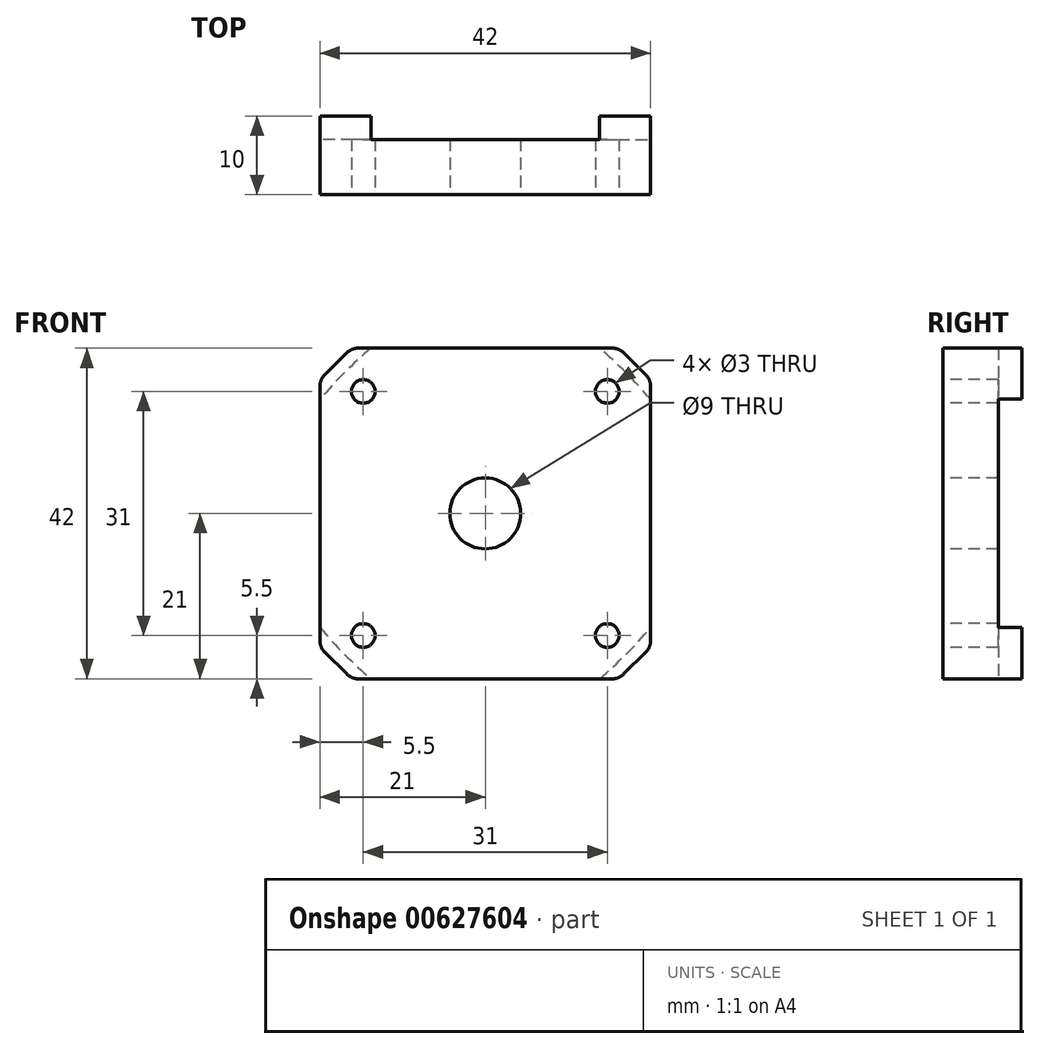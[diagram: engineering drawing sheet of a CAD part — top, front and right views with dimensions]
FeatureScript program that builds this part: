
annotation { "Feature Type Name" : "Feature", "Feature Type Description" : "" }
export const myFeature = defineFeature(function(context is Context, id is Id, definition is map)
    precondition{}
    {
        {
            var Q0;
            Q0=qCreatedBy(makeId("Front.planeOp"),FACE);
            var sketch = newSketch(context, id + "F0", { "sketchPlane" : qUnion([Q0])});
            skLineSegment(sketch, "E0.bottom", {"start": v(-21, 21) * mm, "end": v(21, 21) * mm});
            skLineSegment(sketch, "E0.top", {"start": v(-21, -21) * mm, "end": v(21, -21) * mm});
            skLineSegment(sketch, "E0.left", {"start": v(-21, 21) * mm, "end": v(-21, -21) * mm});
            skLineSegment(sketch, "E0.right", {"start": v(21, 21) * mm, "end": v(21, -21) * mm});
            skPoint(sketch, "E0.middle", {"position": v(0, 0) * mm});
            skSolve(sketch);
        }
        {
            var Q0;
            Q0=makeQuery(id+"F0.imprint","IMPRINT",FACE,{"disambiguationData":[TD([[makeQuery(id+"F0.imprint","IMPRINT",EDGE,{"derivedFrom":sQuery(id+"F0.wireOp",EDGE,"E0.bottom")}),-1.0]])]});
            extrude(context, id + "F1", {"entities" : qUnion([Q0]), "depth" : 10 * mm, "offsetDistance" : 25 * mm});
        }
        {
            var Q0;
            Q0=makeQuery(id+"F1.opExtrude","SWEPT_EDGE",EDGE,{"disambiguationData":[OSD([sQuery(id+"F0.wireOp",EDGE,"E0.bottom"),sQuery(id+"F0.wireOp",EDGE,"E0.left")])]});
            var Q1;
            Q1=makeQuery(id+"F1.opExtrude","SWEPT_EDGE",EDGE,{"disambiguationData":[OSD([sQuery(id+"F0.wireOp",EDGE,"E0.bottom"),sQuery(id+"F0.wireOp",EDGE,"E0.right")])]});
            var Q2;
            Q2=makeQuery(id+"F1.opExtrude","SWEPT_EDGE",EDGE,{"disambiguationData":[OSD([sQuery(id+"F0.wireOp",EDGE,"E0.top"),sQuery(id+"F0.wireOp",EDGE,"E0.right")])]});
            var Q3;
            Q3=makeQuery(id+"F1.opExtrude","SWEPT_EDGE",EDGE,{"disambiguationData":[OSD([sQuery(id+"F0.wireOp",EDGE,"E0.top"),sQuery(id+"F0.wireOp",EDGE,"E0.left")])]});
            chamfer(context, id + "F2", {"entities" : qUnion([Q0, Q1, Q2, Q3]), "width" : 4 * mm, "tangentPropagation" : true});
        }
        {
            var Q0;
            {var subQ0=sQuery(id+"F0.wireOp",EDGE,"E0.bottom");Q0=makeQuery(id+"F2.opChamfer","BLEND_EDGE",EDGE,{"blendedFrom":[makeQuery(id+"F1.opExtrude","SWEPT_EDGE",EDGE,{"disambiguationData":[OSD([subQ0,sQuery(id+"F0.wireOp",EDGE,"E0.left")])]}),makeQuery(id+"F1.opExtrude","SWEPT_FACE",FACE,{"disambiguationData":[OSD([subQ0])]})],"blendedInto":[makeQuery(id+"F1.opExtrude","SWEPT_FACE",FACE,{"disambiguationData":[OSD([subQ0])]})]});}
            var Q1;
            {var subQ0=sQuery(id+"F0.wireOp",EDGE,"E0.bottom");Q1=makeQuery(id+"F2.opChamfer","BLEND_EDGE",EDGE,{"blendedFrom":[makeQuery(id+"F1.opExtrude","SWEPT_EDGE",EDGE,{"disambiguationData":[OSD([subQ0,sQuery(id+"F0.wireOp",EDGE,"E0.right")])]}),makeQuery(id+"F1.opExtrude","SWEPT_FACE",FACE,{"disambiguationData":[OSD([subQ0])]})],"blendedInto":[makeQuery(id+"F1.opExtrude","SWEPT_FACE",FACE,{"disambiguationData":[OSD([subQ0])]})]});}
            var Q2;
            {var subQ0=sQuery(id+"F0.wireOp",EDGE,"E0.right");Q2=makeQuery(id+"F2.opChamfer","BLEND_EDGE",EDGE,{"blendedFrom":[makeQuery(id+"F1.opExtrude","SWEPT_EDGE",EDGE,{"disambiguationData":[OSD([sQuery(id+"F0.wireOp",EDGE,"E0.bottom"),subQ0])]}),makeQuery(id+"F1.opExtrude","SWEPT_FACE",FACE,{"disambiguationData":[OSD([subQ0])]})],"blendedInto":[makeQuery(id+"F1.opExtrude","SWEPT_FACE",FACE,{"disambiguationData":[OSD([subQ0])]})]});}
            var Q3;
            {var subQ0=sQuery(id+"F0.wireOp",EDGE,"E0.right");Q3=makeQuery(id+"F2.opChamfer","BLEND_EDGE",EDGE,{"blendedFrom":[makeQuery(id+"F1.opExtrude","SWEPT_EDGE",EDGE,{"disambiguationData":[OSD([sQuery(id+"F0.wireOp",EDGE,"E0.top"),subQ0])]}),makeQuery(id+"F1.opExtrude","SWEPT_FACE",FACE,{"disambiguationData":[OSD([subQ0])]})],"blendedInto":[makeQuery(id+"F1.opExtrude","SWEPT_FACE",FACE,{"disambiguationData":[OSD([subQ0])]})]});}
            var Q4;
            {var subQ0=sQuery(id+"F0.wireOp",EDGE,"E0.top");Q4=makeQuery(id+"F2.opChamfer","BLEND_EDGE",EDGE,{"blendedFrom":[makeQuery(id+"F1.opExtrude","SWEPT_EDGE",EDGE,{"disambiguationData":[OSD([subQ0,sQuery(id+"F0.wireOp",EDGE,"E0.right")])]}),makeQuery(id+"F1.opExtrude","SWEPT_FACE",FACE,{"disambiguationData":[OSD([subQ0])]})],"blendedInto":[makeQuery(id+"F1.opExtrude","SWEPT_FACE",FACE,{"disambiguationData":[OSD([subQ0])]})]});}
            var Q5;
            {var subQ0=sQuery(id+"F0.wireOp",EDGE,"E0.top");Q5=makeQuery(id+"F2.opChamfer","BLEND_EDGE",EDGE,{"blendedFrom":[makeQuery(id+"F1.opExtrude","SWEPT_EDGE",EDGE,{"disambiguationData":[OSD([subQ0,sQuery(id+"F0.wireOp",EDGE,"E0.left")])]}),makeQuery(id+"F1.opExtrude","SWEPT_FACE",FACE,{"disambiguationData":[OSD([subQ0])]})],"blendedInto":[makeQuery(id+"F1.opExtrude","SWEPT_FACE",FACE,{"disambiguationData":[OSD([subQ0])]})]});}
            var Q6;
            {var subQ0=sQuery(id+"F0.wireOp",EDGE,"E0.left");Q6=makeQuery(id+"F2.opChamfer","BLEND_EDGE",EDGE,{"blendedFrom":[makeQuery(id+"F1.opExtrude","SWEPT_EDGE",EDGE,{"disambiguationData":[OSD([sQuery(id+"F0.wireOp",EDGE,"E0.top"),subQ0])]}),makeQuery(id+"F1.opExtrude","SWEPT_FACE",FACE,{"disambiguationData":[OSD([subQ0])]})],"blendedInto":[makeQuery(id+"F1.opExtrude","SWEPT_FACE",FACE,{"disambiguationData":[OSD([subQ0])]})]});}
            var Q7;
            {var subQ0=sQuery(id+"F0.wireOp",EDGE,"E0.left");Q7=makeQuery(id+"F2.opChamfer","BLEND_EDGE",EDGE,{"blendedFrom":[makeQuery(id+"F1.opExtrude","SWEPT_EDGE",EDGE,{"disambiguationData":[OSD([sQuery(id+"F0.wireOp",EDGE,"E0.bottom"),subQ0])]}),makeQuery(id+"F1.opExtrude","SWEPT_FACE",FACE,{"disambiguationData":[OSD([subQ0])]})],"blendedInto":[makeQuery(id+"F1.opExtrude","SWEPT_FACE",FACE,{"disambiguationData":[OSD([subQ0])]})]});}
            fillet(context, id + "F3", {"entities" : qUnion([Q0, Q1, Q2, Q3, Q4, Q5, Q6, Q7]), "radius" : 2 * mm, "tangentPropagation" : true, "allowEdgeOverflow" : false});
        }
        {
            var Q0;
            Q0=makeQuery(id+"F1.opExtrude","CAP_FACE",FACE,{"disambiguationData":[OSD([sQuery(id+"F0.wireOp",EDGE,"E0.bottom"),sQuery(id+"F0.wireOp",EDGE,"E0.top"),sQuery(id+"F0.wireOp",EDGE,"E0.left"),sQuery(id+"F0.wireOp",EDGE,"E0.right")])],"isStart":true});
            var sketch = newSketch(context, id + "F4", { "sketchPlane" : qUnion([Q0])});
            skLineSegment(sketch, "E1.bottom", {"start": v(-21, 21) * mm, "end": v(21, 21) * mm, "construction": true});
            skLineSegment(sketch, "E1.top", {"start": v(-21, -21) * mm, "end": v(21, -21) * mm, "construction": true});
            skLineSegment(sketch, "E1.left", {"start": v(-21, 21) * mm, "end": v(-21, -21) * mm, "construction": true});
            skLineSegment(sketch, "E1.right", {"start": v(21, 21) * mm, "end": v(21, -21) * mm, "construction": true});
            skPoint(sketch, "E1.middle", {"position": v(0, 0) * mm});
            skArc(sketch, "E2", {"start": v(-21, 14.51) * mm, "mid": v(-17.9, 17.9) * mm, "end": v(-14.51, 21) * mm});
            skArc(sketch, "E3.1.0", {"start": v(-14.51, -21) * mm, "mid": v(-17.9, -17.9) * mm, "end": v(-21, -14.51) * mm});
            skArc(sketch, "E3.2.0", {"start": v(21, -14.51) * mm, "mid": v(17.9, -17.9) * mm, "end": v(14.51, -21) * mm});
            skArc(sketch, "E3.3.0", {"start": v(14.51, 21) * mm, "mid": v(17.9, 17.9) * mm, "end": v(21, 14.51) * mm});
            skLineSegment(sketch, "E4", {"start": v(-21, 14.51) * mm, "end": v(-21, -14.51) * mm});
            skLineSegment(sketch, "E5", {"start": v(-14.51, -21) * mm, "end": v(14.51, -21) * mm});
            skLineSegment(sketch, "E6", {"start": v(21, -14.51) * mm, "end": v(21, 14.51) * mm});
            skLineSegment(sketch, "E7", {"start": v(14.51, 21) * mm, "end": v(-14.51, 21) * mm});
            skSolve(sketch);
        }
        {
            var Q0;
            Q0=qSketchRegion(id+"F4",true);
            extrude(context, id + "F5", {"entities" : qUnion([Q0]), "operationType" : NewBodyOperationType.REMOVE, "oppositeDirection" : true, "depth" : 3 * mm, "offsetDistance" : 25 * mm});
        }
        {
            var Q0;
            Q0=makeQuery(id+"F1.opExtrude","CAP_FACE",FACE,{"disambiguationData":[OSD([sQuery(id+"F0.wireOp",EDGE,"E0.bottom"),sQuery(id+"F0.wireOp",EDGE,"E0.top"),sQuery(id+"F0.wireOp",EDGE,"E0.left"),sQuery(id+"F0.wireOp",EDGE,"E0.right")])],"isStart":false});
            var sketch = newSketch(context, id + "F6", { "sketchPlane" : qUnion([Q0])});
            skCircle(sketch, "E8", {"center": v(-15.5, 15.5) * mm, "radius": 1.5 * mm});
            skCircle(sketch, "E9.1.0", {"center": v(-15.5, -15.5) * mm, "radius": 1.5 * mm});
            skCircle(sketch, "E9.2.0", {"center": v(15.5, -15.5) * mm, "radius": 1.5 * mm});
            skCircle(sketch, "E9.3.0", {"center": v(15.5, 15.5) * mm, "radius": 1.5 * mm});
            skPoint(sketch, "E9.center", {"position": v(0, 0) * mm});
            skSolve(sketch);
        }
        {
            var Q0;
            Q0=qSketchRegion(id+"F6",true);
            extrude(context, id + "F7", {"entities" : qUnion([Q0]), "operationType" : NewBodyOperationType.REMOVE, "endBound" : BoundingType.THROUGH_ALL, "oppositeDirection" : true, "depth" : 25 * mm, "offsetDistance" : 25 * mm});
        }
        {
            var Q0;
            Q0=makeQuery(id+"F1.opExtrude","CAP_FACE",FACE,{"disambiguationData":[OSD([sQuery(id+"F0.wireOp",EDGE,"E0.bottom"),sQuery(id+"F0.wireOp",EDGE,"E0.top"),sQuery(id+"F0.wireOp",EDGE,"E0.left"),sQuery(id+"F0.wireOp",EDGE,"E0.right")])],"isStart":false});
            var sketch = newSketch(context, id + "F8", { "sketchPlane" : qUnion([Q0])});
            skCircle(sketch, "E10", {"center": v(0, 0) * mm, "radius": 4.5 * mm});
            skSolve(sketch);
        }
        {
            var Q0;
            Q0=makeQuery(id+"F8.imprint","IMPRINT",FACE,{"disambiguationData":[TD([[makeQuery(id+"F8.imprint","IMPRINT",EDGE,{"derivedFrom":sQuery(id+"F8.wireOp",EDGE,"E10")}),1.0]])]});
            extrude(context, id + "F9", {"entities" : qUnion([Q0]), "operationType" : NewBodyOperationType.REMOVE, "endBound" : BoundingType.THROUGH_ALL, "oppositeDirection" : true, "depth" : 25 * mm, "offsetDistance" : 25 * mm});
        }
    });
